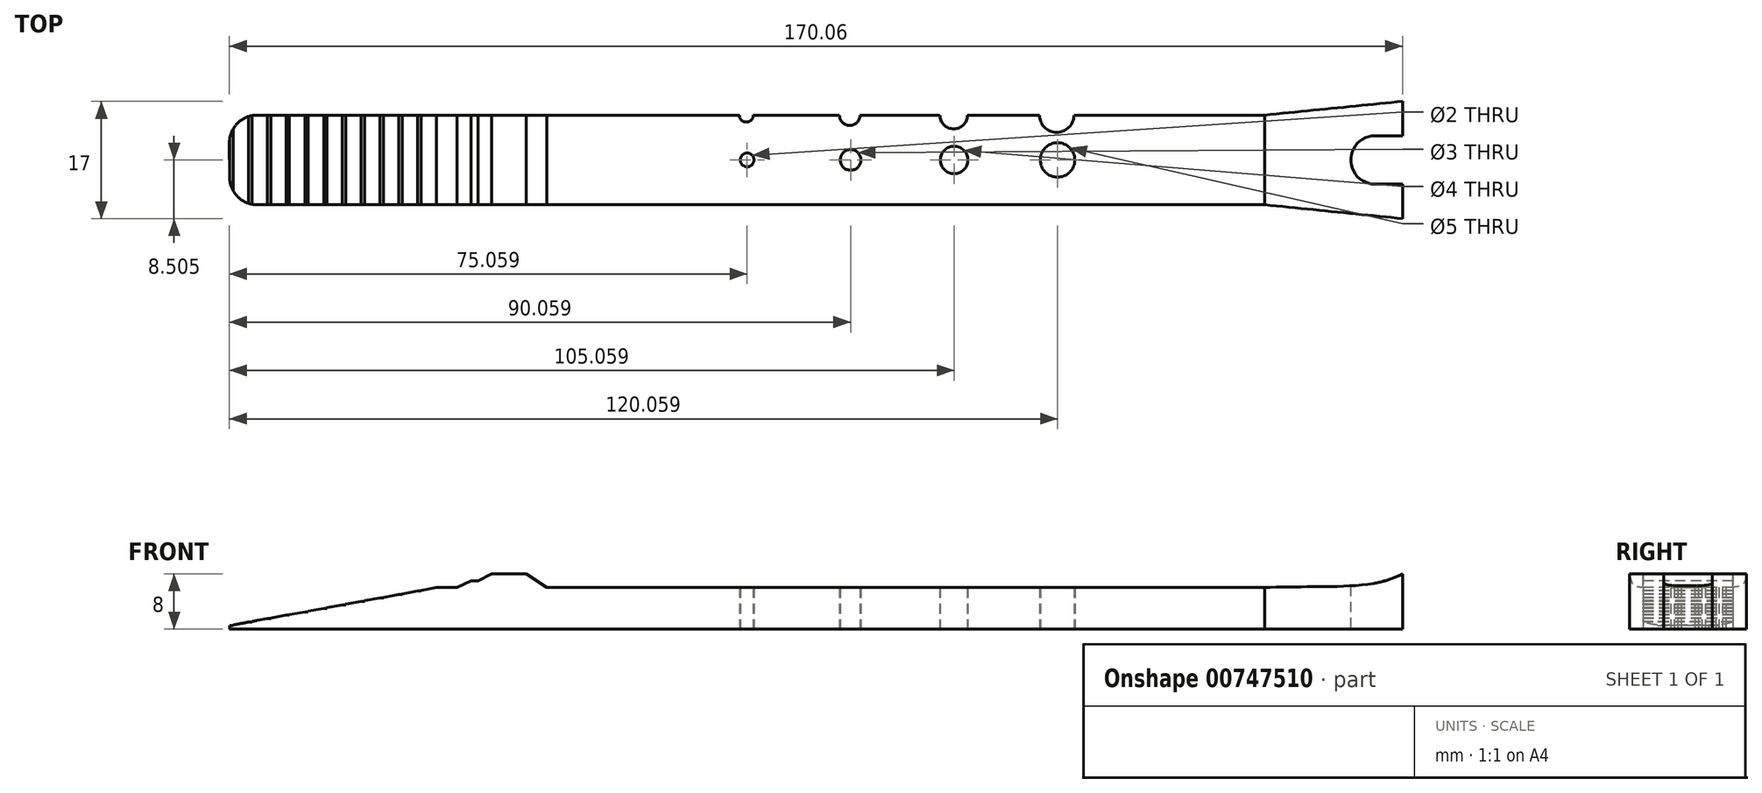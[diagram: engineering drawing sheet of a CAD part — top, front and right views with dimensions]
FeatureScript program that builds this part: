
annotation { "Feature Type Name" : "Feature", "Feature Type Description" : "" }
export const myFeature = defineFeature(function(context is Context, id is Id, definition is map)
    precondition{}
    {
        {
            var Q0;
            Q0=qCreatedBy(makeId("Top.planeOp"),FACE);
            var sketch = newSketch(context, id + "F0", { "sketchPlane" : qUnion([Q0])});
            skLineSegment(sketch, "E0", {"start": v(-98.1, -25.9) * mm, "end": v(47.93, -25.9) * mm});
            skLineSegment(sketch, "E1", {"start": v(47.93, -25.9) * mm, "end": v(47.93, -12.9) * mm});
            skLineSegment(sketch, "E2", {"start": v(47.93, -12.9) * mm, "end": v(20.3, -12.9) * mm});
            skCircle(sketch, "E3", {"center": v(-27.07, -19.4) * mm, "radius": 1 * mm});
            skCircle(sketch, "E4", {"center": v(-12.07, -19.4) * mm, "radius": 1.5 * mm});
            skCircle(sketch, "E5", {"center": v(2.93, -19.4) * mm, "radius": 2 * mm});
            skCircle(sketch, "E6", {"center": v(17.93, -19.4) * mm, "radius": 2.5 * mm});
            skArc(sketch, "E7", {"start": v(-28.2, -12.9) * mm, "mid": v(-27.2, -13.9) * mm, "end": v(-26.2, -12.9) * mm});
            skArc(sketch, "E8", {"start": v(-13.7, -12.9) * mm, "mid": v(-12.2, -14.4) * mm, "end": v(-10.7, -12.9) * mm});
            skArc(sketch, "E9", {"start": v(0.87, -12.9) * mm, "mid": v(2.87, -14.9) * mm, "end": v(4.87, -12.9) * mm});
            skArc(sketch, "E10", {"start": v(15.3, -12.9) * mm, "mid": v(17.8, -15.4) * mm, "end": v(20.3, -12.9) * mm});
            skLineSegment(sketch, "E11.trimOffspring", {"start": v(-28.2, -12.9) * mm, "end": v(-42.2, -12.9) * mm});
            skLineSegment(sketch, "E12.trimOffspring", {"start": v(-13.7, -12.9) * mm, "end": v(-26.2, -12.9) * mm});
            skLineSegment(sketch, "E13.trimOffspring", {"start": v(0.87, -12.9) * mm, "end": v(-10.7, -12.9) * mm});
            skLineSegment(sketch, "E14.trimOffspring", {"start": v(15.3, -12.9) * mm, "end": v(4.87, -12.9) * mm});
            skLineSegment(sketch, "E15", {"start": v(-42.2, -12.9) * mm, "end": v(-98.13, -12.9) * mm});
            skLineSegment(sketch, "E16", {"start": v(-42.2, -12.9) * mm, "end": v(-42.2, -25.9) * mm});
            skLineSegment(sketch, "E17", {"start": v(-102.13, -16.92) * mm, "end": v(-102.1, -21.92) * mm});
            skLineSegment(sketch, "E18", {"start": v(17.93, -19.4) * mm, "end": v(17.93, -25.9) * mm});
            skPoint(sketch, "E19.visualSharp", {"position": v(-102.16, -12.9) * mm});
            skArc(sketch, "E19.filletArc", {"start": v(-98.13, -12.9) * mm, "mid": v(-100.97, -14.07) * mm, "end": v(-102.13, -16.92) * mm});
            skPoint(sketch, "E20.visualSharp", {"position": v(-102.09, -25.9) * mm});
            skArc(sketch, "E20.filletArc", {"start": v(-102.1, -21.92) * mm, "mid": v(-100.93, -24.73) * mm, "end": v(-98.1, -25.9) * mm});
            skSolve(sketch);
        }
        {
            var Q0;
            {var subQ3=sQuery(id+"F0.wireOp",EDGE,"E1");Q0=makeQuery(id+"F0.imprint","IMPRINT",FACE,{"disambiguationData":[TD([[makeQuery(id+"F0.imprint","IMPRINT",EDGE,{"derivedFrom":subQ3}),1.0]])]});}
            var Q1;
            Q1=makeQuery(id+"F0.imprint","IMPRINT",FACE,{"disambiguationData":[TD([[makeQuery(id+"F0.imprint","IMPRINT",EDGE,{"derivedFrom":sQuery(id+"F0.wireOp",EDGE,"E15")}),1.0]])]});
            var Q2;
            Q2=qSketchRegion(id+"F2",true);
            extrude(context, id + "F1", {"entities" : qUnion([Q0, Q1, Q2]), "depth" : 6 * mm, "offsetDistance" : 25 * mm});
        }
        {
            var Q0;
            Q0=makeQuery(id+"F1.opExtrude","CAP_FACE",FACE,{"disambiguationData":[OSD([sQuery(id+"F0.wireOp",EDGE,"uh8EjRIv-oyds-LonH-DEWT-FKtuM7sv1xbY"),sQuery(id+"F0.wireOp",EDGE,"2pE5EAkt-IuKl-0Sab-UQfI-aqEs6KhZttEm"),sQuery(id+"F0.wireOp",EDGE,"Nk6HZn5N-y9iB-Nk6B-fPmU-OZDAcxOevotu"),sQuery(id+"F0.wireOp",EDGE,"LXX49E4n-5PRi-B9FO-bH7N-pa6ycjuBgqBC"),sQuery(id+"F0.wireOp",EDGE,"53KMTElE-K7W9-ORrf-RCAp-qNT4eaaVkteF"),sQuery(id+"F0.wireOp",EDGE,"P7PF4Mbg-ef0C-n9oX-XZ09-ZLFXLgH8y7fW"),sQuery(id+"F0.wireOp",EDGE,"su197C0L-hHtV-Jca1-MSLm-PElzWjnIUR3Y"),sQuery(id+"F0.wireOp",EDGE,"EV9Pacv8-165I-bCM3-OcYT-9LR3dg5SSEyu"),sQuery(id+"F0.wireOp",EDGE,"19IYVO1Q-Y4kt-bx1a-DxFm-OXG8GlXLaGFM"),sQuery(id+"F0.wireOp",EDGE,"65VxX6mh-rfcX-KxfM-GORW-ms9ADtBnMzlR"),sQuery(id+"F0.wireOp",EDGE,"7bQUvBXv-wM8X-eBwg-Mk0h-ePabGQXhmWVm"),sQuery(id+"F0.wireOp",EDGE,"bDx1VqJG-FhMZ-ysIe-255i-NBJnI1b9v1Xd"),sQuery(id+"F0.wireOp",EDGE,"GWuhjFGg-mN8e-GpBZ-US7o-J5IPN2826qVD"),sQuery(id+"F0.wireOp",EDGE,"91LzrW2M-BcOK-ah0N-KhqT-TaDJfhBesgPh"),sQuery(id+"F0.wireOp",EDGE,"1k80qitz-qzns-NigU-Vkyj-1TzsJOIY6Jo9"),sQuery(id+"F0.wireOp",EDGE,"p5sEo6Ta-pkgy-Fa4L-bMfm-GfEhippCeM6v"),sQuery(id+"F0.wireOp",EDGE,"VcT0GBPq-V1kq-JeiP-DT5O-q3OzsVNUBB7H"),sQuery(id+"F0.wireOp",EDGE,"vWu1ZsAQ-pDto-N3AH-TT21-yHdSeIgjR8fg"),sQuery(id+"F0.wireOp",EDGE,"vBJXVKXv-qYgn-2ukd-IsI3-EiIpIBPK8Vaz"),sQuery(id+"F0.wireOp",EDGE,"G37NeImH-WY8i-Es2l-a97g-44kHUUvCxSSy"),sQuery(id+"F0.wireOp",EDGE,"E7LrDzYy-OpsH-mPZP-qLcD-qzzZRt0giBqK"),sQuery(id+"F0.wireOp",EDGE,"s3JVjWtr-fkdu-SgC5-uSSM-x588ayeuHTqY"),sQuery(id+"F0.wireOp",EDGE,"Z1yXTLh1-1L1P-RAfO-bNF2-wSMogvR3wL57"),sQuery(id+"F0.wireOp",EDGE,"ZUVO2fO2-Q0JX-bRAt-EWbK-FMEUTOadSTGL"),sQuery(id+"F0.wireOp",EDGE,"OpzXb7L7-065u-pUx9-msa7-Or2I1k12Jhel"),sQuery(id+"F0.wireOp",EDGE,"E0"),sQuery(id+"F0.wireOp",EDGE,"E1"),sQuery(id+"F0.wireOp",EDGE,"E2"),sQuery(id+"F0.wireOp",EDGE,"E3"),sQuery(id+"F0.wireOp",EDGE,"E4"),sQuery(id+"F0.wireOp",EDGE,"E5"),sQuery(id+"F0.wireOp",EDGE,"E6"),sQuery(id+"F0.wireOp",EDGE,"E7"),sQuery(id+"F0.wireOp",EDGE,"E8"),sQuery(id+"F0.wireOp",EDGE,"E9"),sQuery(id+"F0.wireOp",EDGE,"E10"),sQuery(id+"F0.wireOp",EDGE,"E11.trimOffspring"),sQuery(id+"F0.wireOp",EDGE,"E12.trimOffspring"),sQuery(id+"F0.wireOp",EDGE,"E13.trimOffspring"),sQuery(id+"F0.wireOp",EDGE,"E14.trimOffspring")])],"isStart":true});
            var sketch = newSketch(context, id + "F2", { "sketchPlane" : qUnion([Q0])});
            skLineSegment(sketch, "E21", {"start": v(47.93, 12.9) * mm, "end": v(47.93, 25.9) * mm});
            skLineSegment(sketch, "E22", {"start": v(47.93, 25.9) * mm, "end": v(67.93, 27.9) * mm});
            skLineSegment(sketch, "E23", {"start": v(47.93, 12.9) * mm, "end": v(67.93, 10.9) * mm});
            skLineSegment(sketch, "E24", {"start": v(67.93, 27.9) * mm, "end": v(67.93, 22.9) * mm});
            skLineSegment(sketch, "E25", {"start": v(67.93, 10.9) * mm, "end": v(67.93, 15.9) * mm});
            skLineSegment(sketch, "E26", {"start": v(67.93, 15.9) * mm, "end": v(63.93, 15.9) * mm});
            skLineSegment(sketch, "E27", {"start": v(67.93, 22.9) * mm, "end": v(63.93, 22.9) * mm});
            skArc(sketch, "E28", {"start": v(63.93, 15.9) * mm, "mid": v(60.43, 19.4) * mm, "end": v(63.93, 22.9) * mm});
            skSolve(sketch);
        }
        {
            var Q0;
            Q0=makeQuery(id+"F2.imprint","IMPRINT",FACE,{"disambiguationData":[TD([[makeQuery(id+"F2.imprint","IMPRINT",EDGE,{"derivedFrom":sQuery(id+"F2.wireOp",EDGE,"E21")}),1.0]])]});
            extrude(context, id + "F3", {"entities" : qUnion([Q0]), "operationType" : NewBodyOperationType.ADD, "oppositeDirection" : true, "depth" : 8 * mm, "offsetDistance" : 25 * mm});
        }
        {
            var Q0;
            Q0=makeQuery(id+"F1.opExtrude","SWEPT_FACE",FACE,{"disambiguationData":[OSD([sQuery(id+"F0.wireOp",EDGE,"E0")])]});
            var sketch = newSketch(context, id + "F4", { "sketchPlane" : qUnion([Q0])});
            skFitSpline(sketch, "E29", {"points": [v(47.93, 6) * mm, v(67.93, 8) * mm, v(72.49, 16.65) * mm], "startDerivative": vector(42.2, 1.96) * mm, "endDerivative": vector(-1.7, 25.64) * mm});
            skLineSegment(sketch, "E30", {"start": v(47.93, 21.53) * mm, "end": v(72.53, 21.53) * mm});
            skLineSegment(sketch, "E31", {"start": v(72.53, 21.53) * mm, "end": v(72.53, -3.93) * mm});
            skLineSegment(sketch, "E32", {"start": v(72.53, -3.93) * mm, "end": v(47.93, -3.93) * mm});
            skLineSegment(sketch, "E33", {"start": v(47.93, -3.93) * mm, "end": v(47.93, 0) * mm});
            skLineSegment(sketch, "E34", {"start": v(47.93, 6) * mm, "end": v(46.54, 6) * mm});
            skLineSegment(sketch, "E35", {"start": v(46.54, 6) * mm, "end": v(46.54, 21.53) * mm});
            skLineSegment(sketch, "E36", {"start": v(46.54, 21.53) * mm, "end": v(47.93, 21.53) * mm});
            skLineSegment(sketch, "E37", {"start": v(67.93, 8) * mm, "end": v(67.93, 7.24) * mm});
            skFitSpline(sketch, "E38", {"points": [v(47.93, 0) * mm, v(67.93, 7.24) * mm, v(72.77, 16.03) * mm, v(78.73, 9.87) * mm], "startDerivative": vector(59.64, 6.8) * mm, "endDerivative": vector(27.46, -36.02) * mm});
            skSolve(sketch);
        }
        {
            var Q0;
            Q0=makeQuery(id+"F4.imprint","IMPRINT",FACE,{"disambiguationData":[TD([[makeQuery(id+"F4.imprint","IMPRINT",EDGE,{"derivedFrom":sQuery(id+"F4.wireOp",EDGE,"E30")}),-1.0]])]});
            var Q1;
            {var subQ1=sQuery(id+"F2.wireOp",EDGE,"E22");var subQ2=makeQuery(id+"F3.opExtrude","CAP_EDGE",EDGE,{"disambiguationData":[OSD([subQ1])],"isStart":false});Q1=makeQuery(id+"F4.imprint","IMPRINT",FACE,{"disambiguationData":[TD([[makeQuery(id+"F4.imprint","IMPRINT",EDGE,{"derivedFrom":subQ2}),-1.0]])]});}
            var Q2;
            {var subQ1=sQuery(id+"F2.wireOp",EDGE,"E22");var subQ3=makeQuery(id+"F3.opExtrude","CAP_EDGE",EDGE,{"disambiguationData":[OSD([subQ1])],"isStart":true});Q2=makeQuery(id+"F4.imprint","IMPRINT",FACE,{"disambiguationData":[TD([[makeQuery(id+"F4.imprint","IMPRINT",EDGE,{"derivedFrom":subQ3}),1.0]])]});}
            extrude(context, id + "F5", {"entities" : qUnion([Q0, Q1, Q2]), "operationType" : NewBodyOperationType.REMOVE, "oppositeDirection" : true, "depth" : 25 * mm, "offsetDistance" : 25 * mm, "hasSecondDirection" : true, "secondDirectionOppositeDirection" : false, "secondDirectionDepth" : 25 * mm});
        }
        {
            var Q0;
            Q0=makeQuery(id+"F1.opExtrude","SWEPT_FACE",FACE,{"disambiguationData":[OSD([sQuery(id+"F0.wireOp",EDGE,"E0")])]});
            var sketch = newSketch(context, id + "F6", { "sketchPlane" : qUnion([Q0])});
            skLineSegment(sketch, "E39", {"start": v(-102.1, 0) * mm, "end": v(-102.1, 0.5) * mm});
            skLineSegment(sketch, "E40", {"start": v(-102.1, 0.5) * mm, "end": v(-101.6, 0.5) * mm});
            skLineSegment(sketch, "E41", {"start": v(-72.1, 6) * mm, "end": v(-74.34, 5.6) * mm});
            skLineSegment(sketch, "E42", {"start": v(-101.6, 0.5) * mm, "end": v(-101.6, 0.6) * mm});
            skLineSegment(sketch, "E43", {"start": v(-99.38, 1) * mm, "end": v(-98.88, 1) * mm});
            skLineSegment(sketch, "E44", {"start": v(-98.88, 1) * mm, "end": v(-98.88, 1.1) * mm});
            skLineSegment(sketch, "E45", {"start": v(-96.65, 1.5) * mm, "end": v(-96.15, 1.5) * mm});
            skLineSegment(sketch, "E46", {"start": v(-96.15, 1.5) * mm, "end": v(-96.15, 1.6) * mm});
            skLineSegment(sketch, "E47", {"start": v(-93.93, 2) * mm, "end": v(-93.43, 2) * mm});
            skLineSegment(sketch, "E48", {"start": v(-93.43, 2) * mm, "end": v(-93.43, 2.1) * mm});
            skLineSegment(sketch, "E49", {"start": v(-91.2, 2.5) * mm, "end": v(-90.7, 2.5) * mm});
            skLineSegment(sketch, "E50", {"start": v(-90.7, 2.5) * mm, "end": v(-90.7, 2.6) * mm});
            skLineSegment(sketch, "E51.bottom", {"start": v(-88.47, 3) * mm, "end": v(-87.97, 3) * mm});
            skLineSegment(sketch, "E51.right", {"start": v(-87.97, 3) * mm, "end": v(-87.97, 3.1) * mm});
            skLineSegment(sketch, "E52", {"start": v(-85.75, 3.5) * mm, "end": v(-85.25, 3.5) * mm});
            skLineSegment(sketch, "E53", {"start": v(-85.25, 3.5) * mm, "end": v(-85.25, 3.6) * mm});
            skLineSegment(sketch, "E54", {"start": v(-83.02, 4) * mm, "end": v(-82.52, 4) * mm});
            skLineSegment(sketch, "E55", {"start": v(-82.52, 4) * mm, "end": v(-82.52, 4.1) * mm});
            skLineSegment(sketch, "E56", {"start": v(-80.3, 4.5) * mm, "end": v(-79.8, 4.5) * mm});
            skLineSegment(sketch, "E57", {"start": v(-79.8, 4.5) * mm, "end": v(-79.8, 4.6) * mm});
            skLineSegment(sketch, "E58", {"start": v(-77.56, 5) * mm, "end": v(-77.06, 5) * mm});
            skLineSegment(sketch, "E59", {"start": v(-77.06, 5) * mm, "end": v(-77.06, 5.1) * mm});
            skLineSegment(sketch, "E60", {"start": v(-74.84, 5.5) * mm, "end": v(-74.34, 5.5) * mm});
            skLineSegment(sketch, "E61", {"start": v(-74.34, 5.5) * mm, "end": v(-74.34, 5.6) * mm});
            skLineSegment(sketch, "E62", {"start": v(-71.37, 6.64) * mm, "end": v(-76.82, 6.6) * mm});
            skLineSegment(sketch, "E63", {"start": v(-76.82, 6.6) * mm, "end": v(-98.56, 7.76) * mm});
            skLineSegment(sketch, "E64", {"start": v(-98.56, 7.76) * mm, "end": v(-110.35, 7.76) * mm});
            skLineSegment(sketch, "E65", {"start": v(-110.35, 7.76) * mm, "end": v(-102.1, 0) * mm});
            skLineSegment(sketch, "E66.trimOffspring", {"start": v(-99.38, 1) * mm, "end": v(-101.6, 0.6) * mm});
            skLineSegment(sketch, "E67.trimOffspring", {"start": v(-96.65, 1.5) * mm, "end": v(-98.88, 1.1) * mm});
            skLineSegment(sketch, "E68.trimOffspring", {"start": v(-93.93, 2) * mm, "end": v(-96.15, 1.6) * mm});
            skLineSegment(sketch, "E69.trimOffspring", {"start": v(-91.2, 2.5) * mm, "end": v(-93.43, 2.1) * mm});
            skLineSegment(sketch, "E70.trimOffspring", {"start": v(-88.47, 3) * mm, "end": v(-90.7, 2.6) * mm});
            skLineSegment(sketch, "E71.trimOffspring", {"start": v(-85.75, 3.5) * mm, "end": v(-87.97, 3.1) * mm});
            skLineSegment(sketch, "E72.trimOffspring", {"start": v(-83.02, 4) * mm, "end": v(-85.25, 3.6) * mm});
            skLineSegment(sketch, "E73.trimOffspring", {"start": v(-80.3, 4.5) * mm, "end": v(-82.52, 4.1) * mm});
            skLineSegment(sketch, "E74.trimOffspring", {"start": v(-77.56, 5) * mm, "end": v(-79.8, 4.6) * mm});
            skLineSegment(sketch, "E75.trimOffspring", {"start": v(-74.84, 5.5) * mm, "end": v(-77.06, 5.1) * mm});
            skLineSegment(sketch, "E76", {"start": v(-72.1, 6) * mm, "end": v(-71.37, 6.64) * mm});
            skSolve(sketch);
        }
        {
            var Q0;
            Q0=qSketchRegion(id+"F6",true);
            extrude(context, id + "F7", {"entities" : qUnion([Q0]), "operationType" : NewBodyOperationType.REMOVE, "oppositeDirection" : true, "depth" : 25 * mm, "offsetDistance" : 25 * mm});
        }
        {
            var Q0;
            Q0=makeQuery(id+"F1.opExtrude","SWEPT_FACE",FACE,{"disambiguationData":[OSD([sQuery(id+"F0.wireOp",EDGE,"E0")])]});
            var sketch = newSketch(context, id + "F8", { "sketchPlane" : qUnion([Q0])});
            skLineSegment(sketch, "E77", {"start": v(-69.1, 6) * mm, "end": v(-67.1, 6) * mm});
            skLineSegment(sketch, "E78", {"start": v(-67.1, 7) * mm, "end": v(-66.1, 7) * mm});
            skLineSegment(sketch, "E79", {"start": v(-56.1, 6) * mm, "end": v(-67.1, 6) * mm});
            skLineSegment(sketch, "E80", {"start": v(-69.1, 6) * mm, "end": v(-67.1, 7) * mm});
            skLineSegment(sketch, "E81", {"start": v(-66.1, 7) * mm, "end": v(-64.1, 7) * mm, "construction": true});
            skLineSegment(sketch, "E82", {"start": v(-64.1, 7) * mm, "end": v(-64.1, 8) * mm, "construction": true});
            skLineSegment(sketch, "E83", {"start": v(-66.1, 7) * mm, "end": v(-64.1, 8) * mm});
            skLineSegment(sketch, "E84", {"start": v(-64.1, 8) * mm, "end": v(-59.1, 8) * mm});
            skLineSegment(sketch, "E85", {"start": v(-59.1, 8) * mm, "end": v(-56.1, 6) * mm});
            skSolve(sketch);
        }
        {
            var Q0;
            Q0=makeQuery(id+"F8.imprint","IMPRINT",FACE,{"disambiguationData":[TD([[makeQuery(id+"F8.imprint","IMPRINT",EDGE,{"derivedFrom":sQuery(id+"F8.wireOp",EDGE,"E77")}),1.0]])]});
            extrude(context, id + "F9", {"entities" : qUnion([Q0]), "operationType" : NewBodyOperationType.ADD, "oppositeDirection" : true, "depth" : 13 * mm, "offsetDistance" : 25 * mm});
        }
    });
